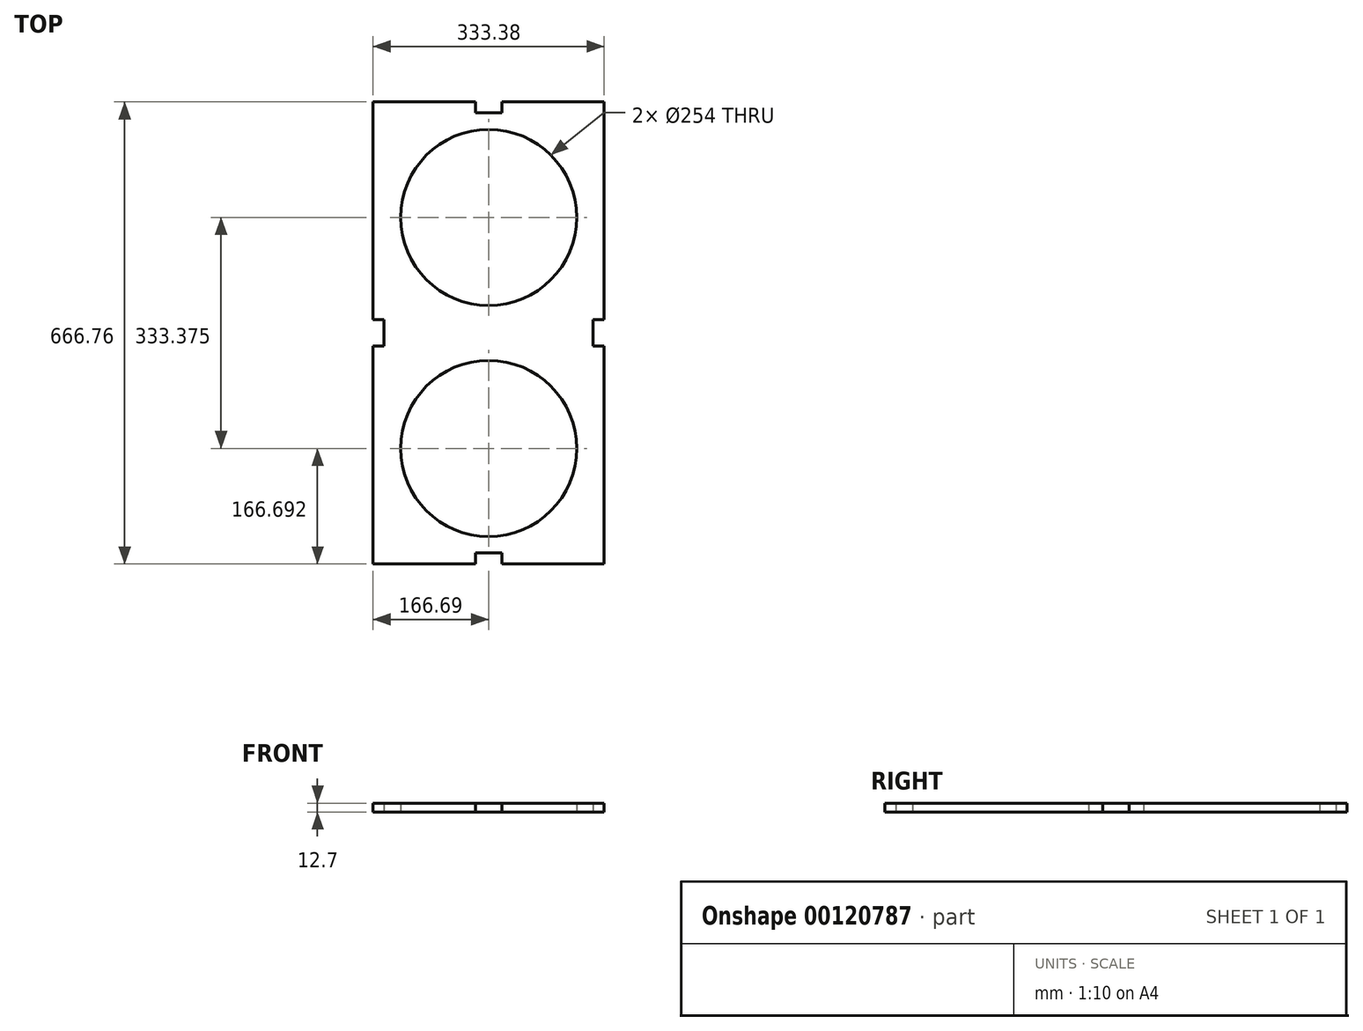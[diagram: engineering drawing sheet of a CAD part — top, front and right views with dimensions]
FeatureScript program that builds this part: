
annotation { "Feature Type Name" : "Feature", "Feature Type Description" : "" }
export const myFeature = defineFeature(function(context is Context, id is Id, definition is map)
    precondition{}
    {
        {
            var Q0;
            Q0=qCreatedBy(makeId("Top.planeOp"),FACE);
            var sketch = newSketch(context, id + "F0", { "sketchPlane" : qUnion([Q0])});
            skLineSegment(sketch, "E0.bottom", {"start": v(166.69, -166.69) * mm, "end": v(-166.69, -166.69) * mm});
            skLineSegment(sketch, "E0.top", {"start": v(166.69, 166.69) * mm, "end": v(-166.69, 166.69) * mm});
            skLineSegment(sketch, "E0.left", {"start": v(166.69, -166.69) * mm, "end": v(166.69, 166.69) * mm});
            skLineSegment(sketch, "E0.right", {"start": v(-166.69, -166.69) * mm, "end": v(-166.69, 166.69) * mm});
            skPoint(sketch, "E0.middle", {"position": v(0, 0) * mm});
            skCircle(sketch, "E1", {"center": v(0, -166.69) * mm, "radius": 127 * mm});
            skCircle(sketch, "E2", {"center": v(0, 166.69) * mm, "radius": 127 * mm});
            skLineSegment(sketch, "E3.bottom", {"start": v(-166.69, -19.05) * mm, "end": v(-150.81, -19.05) * mm});
            skLineSegment(sketch, "E3.top", {"start": v(-166.69, 19.05) * mm, "end": v(-150.81, 19.05) * mm});
            skLineSegment(sketch, "E3.left", {"start": v(-166.69, -19.05) * mm, "end": v(-166.69, 19.05) * mm});
            skLineSegment(sketch, "E3.right", {"start": v(-150.81, -19.05) * mm, "end": v(-150.81, 19.05) * mm});
            skPoint(sketch, "E3.middle", {"position": v(-158.75, 0) * mm});
            skPoint(sketch, "E3.middle.positionSnap0", {"position": v(-166.69, 0) * mm});
            skPoint(sketch, "E3.centerSnap0", {"position": v(-166.69, 0) * mm});
            skPoint(sketch, "E4.MirrorP", {"position": v(166.69, 0) * mm});
            skLineSegment(sketch, "E5.MirrorCS", {"start": v(166.69, -19.05) * mm, "end": v(150.81, -19.05) * mm});
            skPoint(sketch, "E6.MirrorP", {"position": v(158.75, 0) * mm});
            skLineSegment(sketch, "E7.MirrorCS", {"start": v(150.81, -19.05) * mm, "end": v(150.81, 19.05) * mm});
            skLineSegment(sketch, "E8.MirrorCS", {"start": v(166.69, -19.05) * mm, "end": v(166.69, 19.05) * mm});
            skLineSegment(sketch, "E9.MirrorCS", {"start": v(166.69, 19.05) * mm, "end": v(150.81, 19.05) * mm});
            skLineSegment(sketch, "E10.bottom", {"start": v(19.05, 333.38) * mm, "end": v(-19.05, 333.38) * mm});
            skLineSegment(sketch, "E10.top", {"start": v(19.05, 317.5) * mm, "end": v(-19.05, 317.5) * mm});
            skLineSegment(sketch, "E10.left", {"start": v(19.05, 333.38) * mm, "end": v(19.05, 317.5) * mm});
            skLineSegment(sketch, "E10.right", {"start": v(-19.05, 333.38) * mm, "end": v(-19.05, 317.5) * mm});
            skPoint(sketch, "E10.middle", {"position": v(0, 325.44) * mm});
            skLineSegment(sketch, "E11.MirrorCS", {"start": v(19.05, -333.38) * mm, "end": v(-19.05, -333.38) * mm});
            skLineSegment(sketch, "E12.MirrorCS", {"start": v(19.05, -333.38) * mm, "end": v(19.05, -317.5) * mm});
            skPoint(sketch, "E13.MirrorP", {"position": v(0, -325.44) * mm});
            skLineSegment(sketch, "E14.MirrorCS", {"start": v(-19.05, -333.38) * mm, "end": v(-19.05, -317.5) * mm});
            skLineSegment(sketch, "E15.MirrorCS", {"start": v(19.05, -317.5) * mm, "end": v(-19.05, -317.5) * mm});
            skLineSegment(sketch, "E16.bottom", {"start": v(166.69, -333.38) * mm, "end": v(-166.69, -333.38) * mm});
            skLineSegment(sketch, "E16.top", {"start": v(166.69, 333.38) * mm, "end": v(-166.69, 333.38) * mm});
            skLineSegment(sketch, "E16.left", {"start": v(166.69, -333.38) * mm, "end": v(166.69, 333.38) * mm});
            skLineSegment(sketch, "E16.right", {"start": v(-166.69, -333.38) * mm, "end": v(-166.69, 333.38) * mm});
            skSolve(sketch);
        }
        {
            var Q0;
            {var subQ1=sQuery(id+"F0.wireOp",EDGE,"E0.bottom");var subQ3=sQuery(id+"F0.wireOp",EDGE,"E1");var subQ4=makeQuery(id+"F0.imprint","INTERSECT",VERTEX,{"disambiguationData":[OD(0.0)],"derivedFrom":[subQ1,subQ3]});Q0=makeQuery(id+"F0.imprint","IMPRINT",FACE,{"disambiguationData":[TD([[makeQuery(id+"F0.imprint","IMPRINT",EDGE,{"disambiguationData":[TD([[subQ4,1.0]])],"derivedFrom":subQ3}),-1.0]])]});}
            var Q1;
            {var subQ1=sQuery(id+"F0.wireOp",EDGE,"E0.top");var subQ3=sQuery(id+"F0.wireOp",EDGE,"E2");var subQ4=makeQuery(id+"F0.imprint","INTERSECT",VERTEX,{"disambiguationData":[OD(0.0)],"derivedFrom":[subQ1,subQ3]});Q1=makeQuery(id+"F0.imprint","IMPRINT",FACE,{"disambiguationData":[TD([[makeQuery(id+"F0.imprint","IMPRINT",EDGE,{"disambiguationData":[TD([[subQ4,-1.0]])],"derivedFrom":subQ3}),-1.0]])]});}
            var Q2;
            {var subQ0=sQuery(id+"F0.wireOp",EDGE,"E0.right");Q2=makeQuery(id+"F0.imprint","IMPRINT",FACE,{"disambiguationData":[TD([[makeQuery(id+"F0.imprint","IMPRINT",EDGE,{"derivedFrom":subQ0}),-1.0]])]});}
            var Q3;
            {var subQ1=sQuery(id+"F0.wireOp",EDGE,"E0.bottom");var subQ4=sQuery(id+"F0.wireOp",EDGE,"E1");var subQ7=makeQuery(id+"F0.imprint","INTERSECT",VERTEX,{"disambiguationData":[OD(0.0)],"derivedFrom":[subQ1,subQ4]});Q3=makeQuery(id+"F0.imprint","IMPRINT",FACE,{"disambiguationData":[TD([[makeQuery(id+"F0.imprint","IMPRINT",EDGE,{"disambiguationData":[TD([[subQ7,-1.0]])],"derivedFrom":subQ4}),-1.0]])]});}
            var Q4;
            {var subQ1=sQuery(id+"F0.wireOp",EDGE,"E0.top");var subQ4=sQuery(id+"F0.wireOp",EDGE,"E2");var subQ5=makeQuery(id+"F0.imprint","INTERSECT",VERTEX,{"disambiguationData":[OD(0.0)],"derivedFrom":[subQ1,subQ4]});Q4=makeQuery(id+"F0.imprint","IMPRINT",FACE,{"disambiguationData":[TD([[makeQuery(id+"F0.imprint","IMPRINT",EDGE,{"disambiguationData":[TD([[subQ5,1.0]])],"derivedFrom":subQ4}),-1.0]])]});}
            var Q5;
            {var subQ0=sQuery(id+"F0.wireOp",EDGE,"E0.left");Q5=makeQuery(id+"F0.imprint","IMPRINT",FACE,{"disambiguationData":[TD([[makeQuery(id+"F0.imprint","IMPRINT",EDGE,{"derivedFrom":subQ0}),1.0]])]});}
            var Q6;
            {var subQ1=sQuery(id+"F0.wireOp",EDGE,"E3.bottom");Q6=makeQuery(id+"F0.imprint","IMPRINT",FACE,{"disambiguationData":[TD([[makeQuery(id+"F0.imprint","IMPRINT",EDGE,{"derivedFrom":subQ1}),-1.0]])]});}
            var Q7;
            {var subQ0=sQuery(id+"F0.wireOp",EDGE,"E5.MirrorCS");Q7=makeQuery(id+"F0.imprint","IMPRINT",FACE,{"disambiguationData":[TD([[makeQuery(id+"F0.imprint","IMPRINT",EDGE,{"derivedFrom":subQ0}),1.0]])]});}
            var Q8;
            {var subQ0=sQuery(id+"F0.wireOp",EDGE,"E16.left");var subQ4=sQuery(id+"F0.wireOp",EDGE,"E16.top");var subQ6=makeQuery(id+"F0.imprint","INTERSECT",VERTEX,{"derivedFrom":[subQ4,subQ0]});Q8=makeQuery(id+"F0.imprint","IMPRINT",FACE,{"disambiguationData":[TD([[makeQuery(id+"F0.imprint","IMPRINT",EDGE,{"disambiguationData":[TD([[subQ6,-1.0]])],"derivedFrom":subQ4}),1.0]])]});}
            var Q9;
            {var subQ2=sQuery(id+"F0.wireOp",EDGE,"E16.top");var subQ4=sQuery(id+"F0.wireOp",EDGE,"E16.right");var subQ6=makeQuery(id+"F0.imprint","INTERSECT",VERTEX,{"derivedFrom":[subQ2,subQ4]});Q9=makeQuery(id+"F0.imprint","IMPRINT",FACE,{"disambiguationData":[TD([[makeQuery(id+"F0.imprint","IMPRINT",EDGE,{"disambiguationData":[TD([[subQ6,1.0]])],"derivedFrom":subQ2}),1.0]])]});}
            var Q10;
            {var subQ2=sQuery(id+"F0.wireOp",EDGE,"E16.bottom");var subQ4=sQuery(id+"F0.wireOp",EDGE,"E16.left");var subQ6=makeQuery(id+"F0.imprint","INTERSECT",VERTEX,{"derivedFrom":[subQ2,subQ4]});Q10=makeQuery(id+"F0.imprint","IMPRINT",FACE,{"disambiguationData":[TD([[makeQuery(id+"F0.imprint","IMPRINT",EDGE,{"disambiguationData":[TD([[subQ6,-1.0]])],"derivedFrom":subQ2}),-1.0]])]});}
            var Q11;
            {var subQ0=sQuery(id+"F0.wireOp",EDGE,"E16.right");var subQ4=sQuery(id+"F0.wireOp",EDGE,"E16.bottom");var subQ6=makeQuery(id+"F0.imprint","INTERSECT",VERTEX,{"derivedFrom":[subQ4,subQ0]});Q11=makeQuery(id+"F0.imprint","IMPRINT",FACE,{"disambiguationData":[TD([[makeQuery(id+"F0.imprint","IMPRINT",EDGE,{"disambiguationData":[TD([[subQ6,1.0]])],"derivedFrom":subQ4}),-1.0]])]});}
            extrude(context, id + "F1", {"entities" : qUnion([Q0, Q1, Q2, Q3, Q4, Q5, Q6, Q7, Q8, Q9, Q10, Q11]), "depth" : 12.7 * mm});
        }
    });
